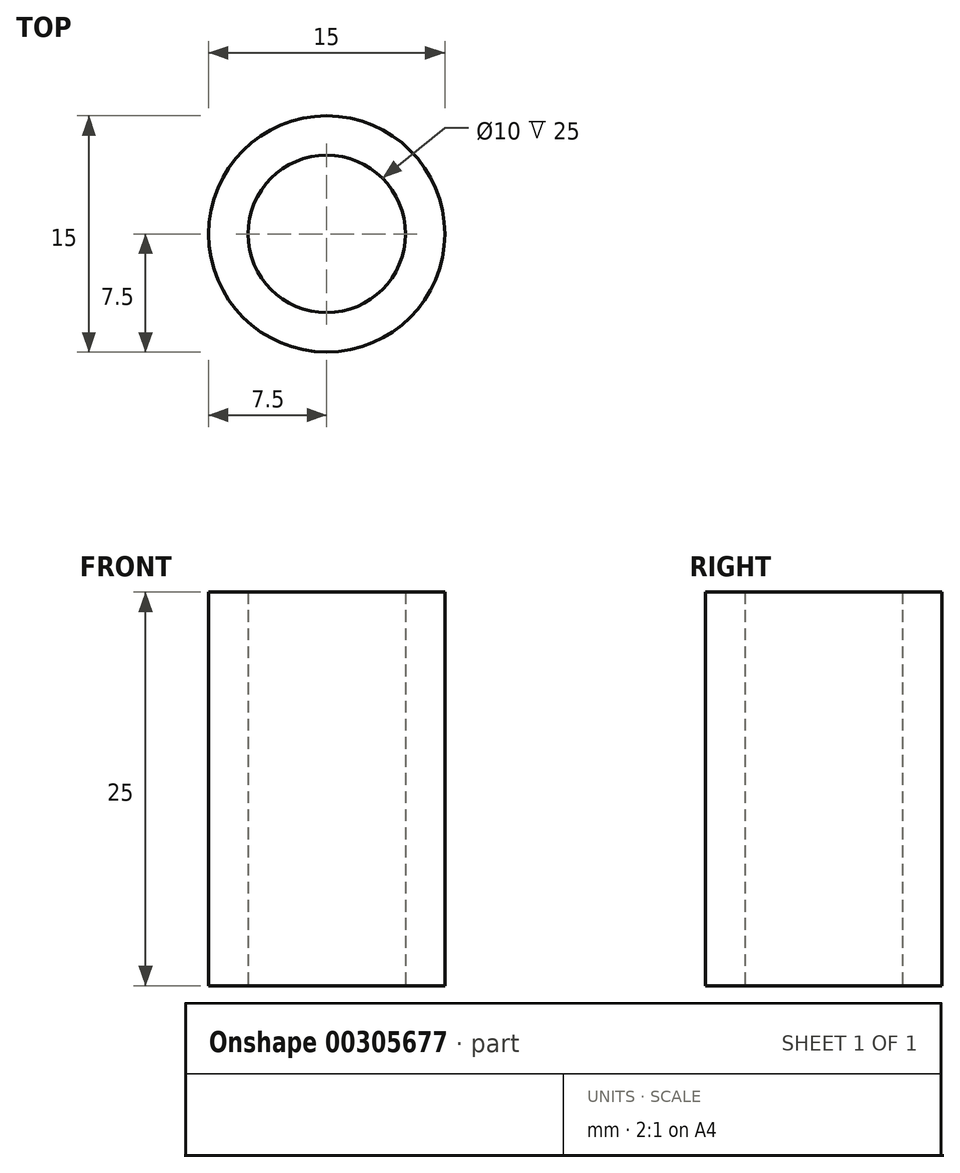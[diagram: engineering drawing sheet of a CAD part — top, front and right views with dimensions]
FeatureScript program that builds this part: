
annotation { "Feature Type Name" : "Feature", "Feature Type Description" : "" }
export const myFeature = defineFeature(function(context is Context, id is Id, definition is map)
    precondition{}
    {
        {
            var Q0;
            Q0=qCreatedBy(makeId("Top.planeOp"),FACE);
            var sketch = newSketch(context, id + "F0", { "sketchPlane" : qUnion([Q0])});
            skCircle(sketch, "E0", {"center": v(0, 0) * mm, "radius": 7.5 * mm});
            skCircle(sketch, "E1", {"center": v(0, 0) * mm, "radius": 5 * mm});
            skLineSegment(sketch, "E2", {"start": v(0, 7.5) * mm, "end": v(0, -7.5) * mm, "construction": true});
            skSolve(sketch);
        }
        {
            var Q0;
            Q0 = qSketchRegion(id + "F0", true);
            extrude(context, id + "F1", {"entities" : qUnion([Q0]), "depth" : 25 * mm});
        }
        {
            var Q0;
            Q0=qCreatedBy(makeId("Front.planeOp"),FACE);
            cPlane(context, id + "F2", {"entities" : qUnion([Q0]), "cplaneType" : CPlaneType.OFFSET, "offset" : (15 / 2) * mm, "width" : 150 * mm, "height" : 150 * mm});
        }
    });
